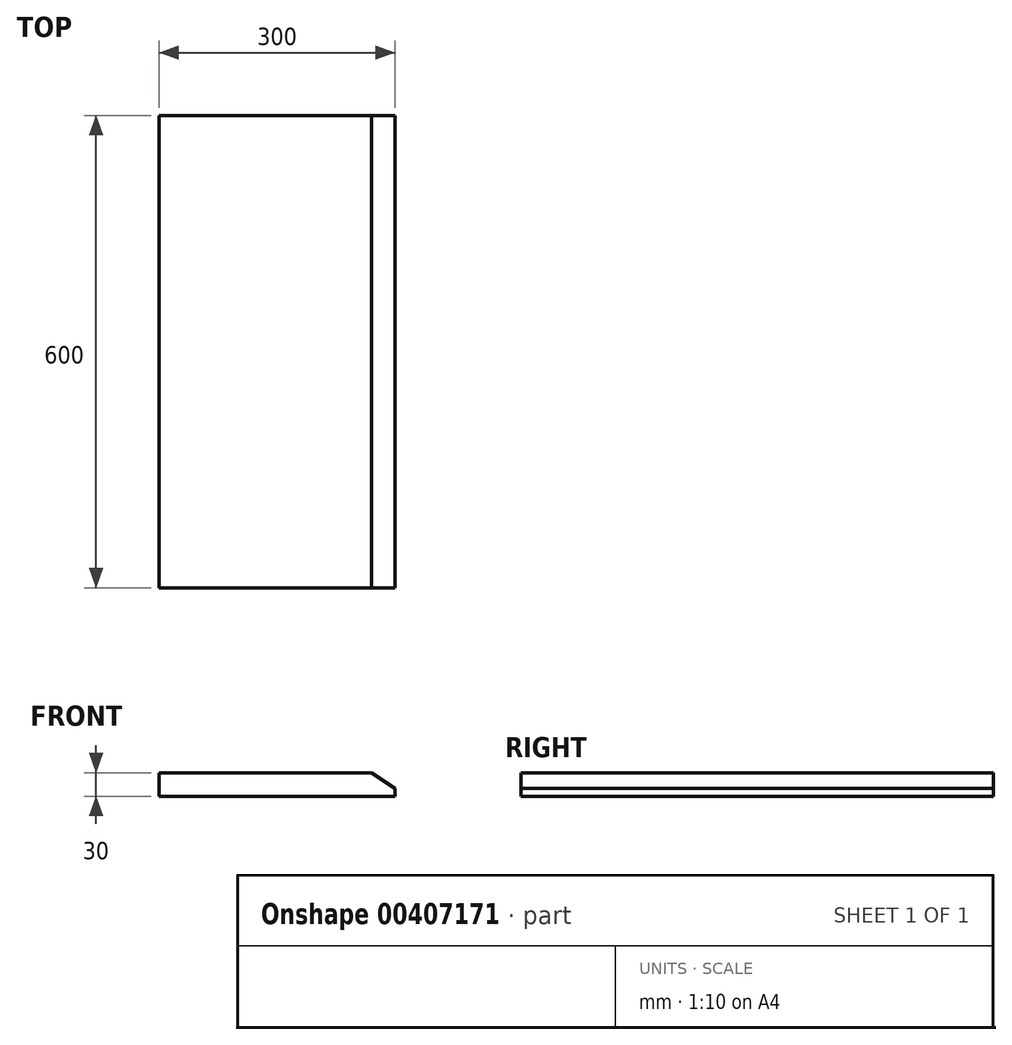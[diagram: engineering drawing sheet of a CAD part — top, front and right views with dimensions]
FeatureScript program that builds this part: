
annotation { "Feature Type Name" : "Feature", "Feature Type Description" : "" }
export const myFeature = defineFeature(function(context is Context, id is Id, definition is map)
    precondition{}
    {
        {
            var Q0;
            Q0=qCreatedBy(makeId("Front.planeOp"),FACE);
            var sketch = newSketch(context, id + "F0", { "sketchPlane" : qUnion([Q0])});
            skLineSegment(sketch, "E0.bottom", {"start": v(0, 0) * mm, "end": v(-300, 0) * mm});
            skLineSegment(sketch, "E0.top", {"start": v(-30, 30) * mm, "end": v(-300, 30) * mm});
            skLineSegment(sketch, "E0.left", {"start": v(0, 0) * mm, "end": v(0, 10) * mm});
            skLineSegment(sketch, "E0.right", {"start": v(-300, 0) * mm, "end": v(-300, 30) * mm});
            skLineSegment(sketch, "E1", {"start": v(0, 10) * mm, "end": v(-30, 30) * mm});
            skPoint(sketch, "E2.orphan", {"position": v(0, 30) * mm});
            skSolve(sketch);
        }
        {
            var Q0;
            Q0=makeQuery(id+"F0.imprint","IMPRINT",FACE,{"disambiguationData":[TD([[makeQuery(id+"F0.imprint","IMPRINT",EDGE,{"derivedFrom":sQuery(id+"F0.wireOp",EDGE,"E0.bottom")}),-1.0]])]});
            extrude(context, id + "F1", {"entities" : qUnion([Q0]), "depth" : 600 * mm, "offsetDistance" : 25 * mm});
        }
    });
